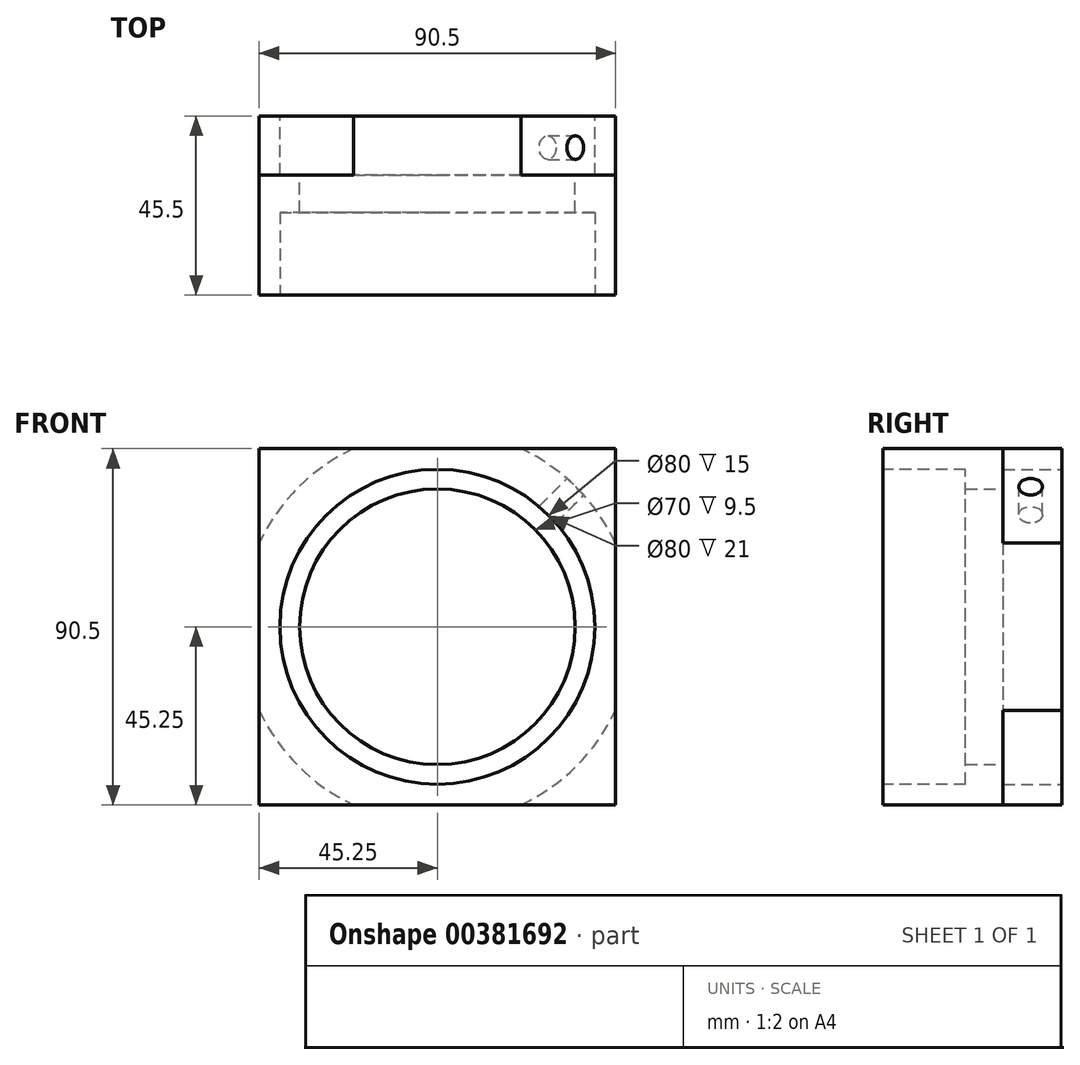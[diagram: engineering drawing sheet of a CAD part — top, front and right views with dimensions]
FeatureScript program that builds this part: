
annotation { "Feature Type Name" : "Feature", "Feature Type Description" : "" }
export const myFeature = defineFeature(function(context is Context, id is Id, definition is map)
    precondition{}
    {
        {
            var Q0;
            Q0=qCreatedBy(makeId("Front.planeOp"),FACE);
            var sketch = newSketch(context, id + "F0", { "sketchPlane" : qUnion([Q0])});
            skLineSegment(sketch, "E0.bottom", {"start": v(-45.25, -45.25) * mm, "end": v(45.25, -45.25) * mm});
            skLineSegment(sketch, "E0.top", {"start": v(-45.25, 45.25) * mm, "end": v(45.25, 45.25) * mm});
            skLineSegment(sketch, "E0.left", {"start": v(-45.25, -45.25) * mm, "end": v(-45.25, 45.25) * mm});
            skLineSegment(sketch, "E0.right", {"start": v(45.25, -45.25) * mm, "end": v(45.25, 45.25) * mm});
            skPoint(sketch, "E0.middle", {"position": v(0, 0) * mm});
            skSolve(sketch);
        }
        {
            var Q0;
            Q0 = qSketchRegion(id + "F0", true);
            extrude(context, id + "F1", {"entities" : qUnion([Q0]), "depth" : 45.5 * mm});
        }
        {
            var Q0;
            Q0=makeQuery(id+"F1.opExtrude","CAP_FACE",FACE,{"disambiguationData":[OSD([sQuery(id+"F0.wireOp",EDGE,"E0.bottom"),sQuery(id+"F0.wireOp",EDGE,"E0.top"),sQuery(id+"F0.wireOp",EDGE,"E0.left"),sQuery(id+"F0.wireOp",EDGE,"E0.right")])],"isStart":true});
            var sketch = newSketch(context, id + "F2", { "sketchPlane" : qUnion([Q0])});
            skCircle(sketch, "E1", {"center": v(0, 0) * mm, "radius": 40 * mm});
            skSolve(sketch);
        }
        {
            var Q0;
            Q0 = qSketchRegion(id + "F2", true);
            extrude(context, id + "F3", {"entities" : qUnion([Q0]), "operationType" : NewBodyOperationType.REMOVE, "oppositeDirection" : true, "depth" : 15 * mm});
        }
        {
            var Q0;
            Q0=makeQuery(id+"F3.boolean.opBoolean","COPY",FACE,{"derivedFrom":makeQuery(id+"F3.opExtrude","CAP_FACE",FACE,{"disambiguationData":[OSD([sQuery(id+"F2.wireOp",EDGE,"E1")])],"isStart":false})});
            var sketch = newSketch(context, id + "F4", { "sketchPlane" : qUnion([Q0])});
            skCircle(sketch, "E2", {"center": v(0, 0) * mm, "radius": 35 * mm});
            skSolve(sketch);
        }
        {
            var Q0;
            Q0 = qSketchRegion(id + "F4", true);
            extrude(context, id + "F5", {"entities" : qUnion([Q0]), "operationType" : NewBodyOperationType.REMOVE, "oppositeDirection" : true, "depth" : 25 * mm});
        }
        {
            var Q0;
            Q0=makeQuery(id+"F1.opExtrude","CAP_FACE",FACE,{"disambiguationData":[OSD([sQuery(id+"F0.wireOp",EDGE,"E0.bottom"),sQuery(id+"F0.wireOp",EDGE,"E0.top"),sQuery(id+"F0.wireOp",EDGE,"E0.left"),sQuery(id+"F0.wireOp",EDGE,"E0.right")])],"isStart":false});
            var sketch = newSketch(context, id + "F6", { "sketchPlane" : qUnion([Q0])});
            skCircle(sketch, "E3", {"center": v(0, 0) * mm, "radius": 40 * mm});
            skSolve(sketch);
        }
        {
            var Q0;
            Q0 = qSketchRegion(id + "F6", true);
            extrude(context, id + "F7", {"entities" : qUnion([Q0]), "operationType" : NewBodyOperationType.REMOVE, "oppositeDirection" : true, "depth" : 21 * mm});
        }
        {
            var Q0;
            Q0=makeQuery(id+"F1.opExtrude","CAP_FACE",FACE,{"disambiguationData":[OSD([sQuery(id+"F0.wireOp",EDGE,"E0.bottom"),sQuery(id+"F0.wireOp",EDGE,"E0.top"),sQuery(id+"F0.wireOp",EDGE,"E0.left"),sQuery(id+"F0.wireOp",EDGE,"E0.right")])],"isStart":true});
            var sketch = newSketch(context, id + "F8", { "sketchPlane" : qUnion([Q0])});
            skCircle(sketch, "E4", {"center": v(0, 0) * mm, "radius": 72.4 * mm});
            skCircle(sketch, "E5", {"center": v(0, 0) * mm, "radius": 50 * mm});
            skSolve(sketch);
        }
        {
            var Q0;
            Q0 = qSketchRegion(id + "F8", true);
            extrude(context, id + "F9", {"entities" : qUnion([Q0]), "operationType" : NewBodyOperationType.REMOVE, "oppositeDirection" : true, "depth" : 15 * mm, "offsetDistance" : 25 * mm});
        }
        {
            var Q0;
            Q0=makeQuery(id+"F1.opExtrude","CAP_FACE",FACE,{"disambiguationData":[OSD([sQuery(id+"F0.wireOp",EDGE,"E0.bottom"),sQuery(id+"F0.wireOp",EDGE,"E0.top"),sQuery(id+"F0.wireOp",EDGE,"E0.left"),sQuery(id+"F0.wireOp",EDGE,"E0.right")])],"isStart":true});
            cPlane(context, id + "F10", {"entities" : qUnion([Q0]), "cplaneType" : CPlaneType.OFFSET, "offset" : 8 * mm, "oppositeDirection" : true, "width" : 150 * mm, "height" : 150 * mm});
        }
        {
            var Q0;
            Q0=qCreatedBy(id+"F10.planeOp",FACE);
            var sketch = newSketch(context, id + "F11", { "sketchPlane" : qUnion([Q0])});
            skLineSegment(sketch, "E6", {"start": v(0, 0) * mm, "end": v(-45.15, 45.86) * mm});
            skLineSegment(sketch, "E7.0", {"start": v(2.14, 2.1) * mm, "end": v(-43.01, 47.97) * mm});
            skLineSegment(sketch, "E8", {"start": v(-43.01, 47.97) * mm, "end": v(-45.15, 45.86) * mm});
            skLineSegment(sketch, "E9", {"start": v(0, 0) * mm, "end": v(2.14, 2.1) * mm});
            skSolve(sketch);
        }
        {
            var Q0;
            Q0=makeQuery(id+"F11.imprint","IMPRINT",FACE,{"disambiguationData":[TD([[makeQuery(id+"F11.imprint","IMPRINT",EDGE,{"derivedFrom":sQuery(id+"F11.wireOp",EDGE,"E6")}),-1.0]])]});
            var Q1;
            Q1=sQuery(id+"F11.wireOp",EDGE,"E6");
            revolve(context, id + "F12", {"operationType" : NewBodyOperationType.REMOVE, "surfaceOperationType" : NewSurfaceOperationType.NEW, "entities" : qUnion([Q0]), "axis" : qUnion([Q1]), "revolveType" : RevolveType.FULL, "oppositeDirection" : true});
        }
    });
